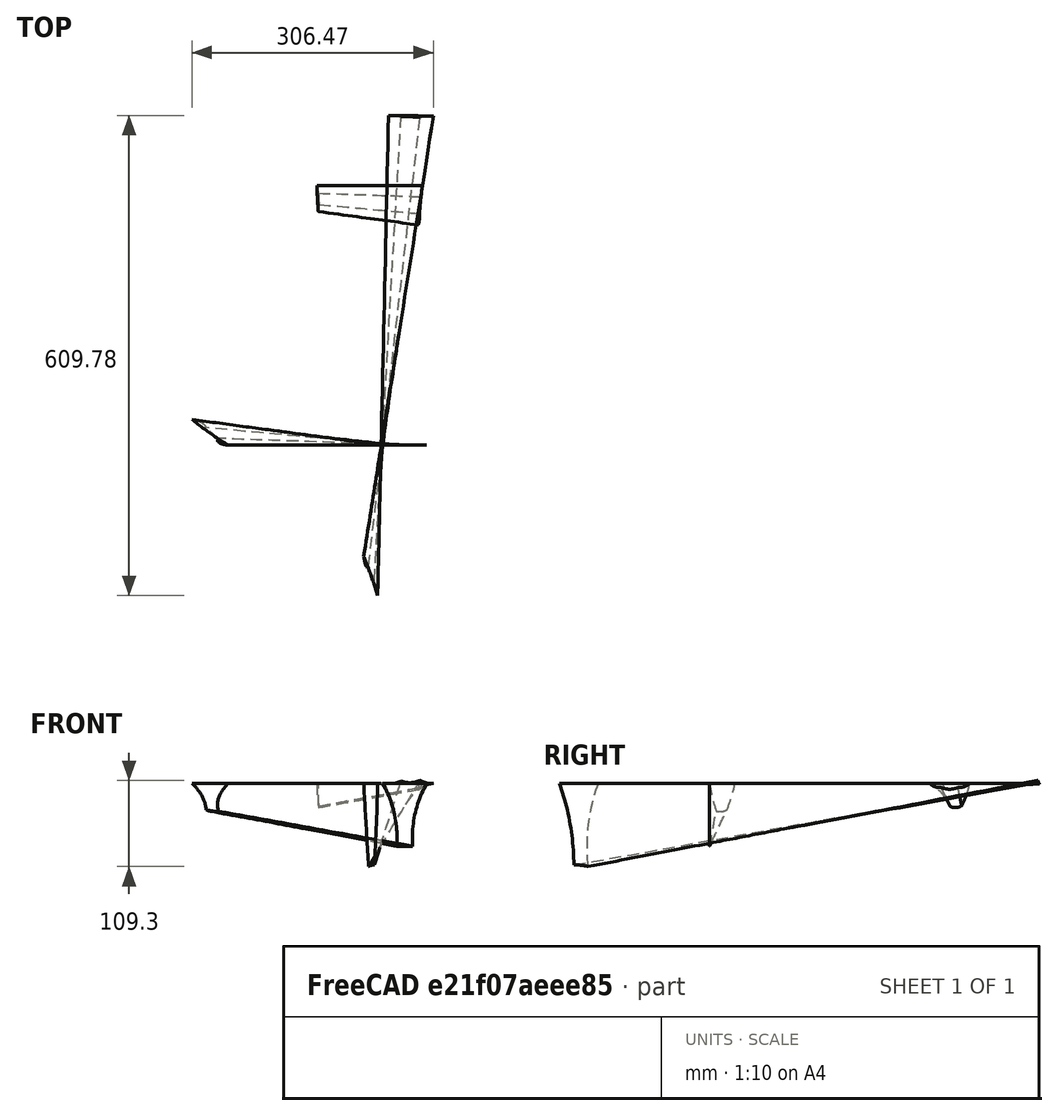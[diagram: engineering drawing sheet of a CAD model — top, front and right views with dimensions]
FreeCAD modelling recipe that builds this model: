
FCSTD DOCUMENT  (FreeCAD 0.19R24291 (Git))
Label: Neck
License: All rights reserved
LicenseURL: http://en.wikipedia.org/wiki/All_rights_reserved
objects: Sketcher::SketchObject×5, PartDesign::Body×1, Part::Sweep×1
note: 7 computed .brp shape members not serialized (recipe doc carries the construction recipe); baked Part::Feature solids carry a one-line shape summary decoded from their .brp

FEATURE [Sketcher::SketchObject] Sketch001  label="Neck_Profile_001"
  FullyConstrained = true
  Placement = pos=(0,0,0) rot=(1,0,0;1.5708rad)
  sketch-geometry (10):
    g0: GeomPoint X=-28 Y=-1.56319e-11 Z=0
    g1: GeomPoint X=28 Y=-1.56746e-11 Z=0
    g2: LineSegment StartX=-28 StartY=-1.56319e-11 StartZ=0 EndX=28 EndY=-1.56746e-11 EndZ=0
    g3: GeomPoint X=-10 Y=-80 Z=0
    g4: GeomPoint X=10 Y=-80 Z=0
    g5: LineSegment StartX=-10 StartY=-80 StartZ=0 EndX=10 EndY=-80 EndZ=0
    g6: GeomPoint X=-10 Y=-60 Z=0
    g7: GeomPoint X=10 Y=-60 Z=0
    g8: ArcOfCircle CenterX=-152.333 CenterY=-70 CenterZ=0 NormalX=0 NormalY=0 NormalZ=1 AngleXU=0 Radius=142.684 StartAngle=6.21304 EndAngle=6.79596
    g9: ArcOfCircle CenterX=152.333 CenterY=-70 CenterZ=0 NormalX=0 NormalY=0 NormalZ=1 AngleXU=0 Radius=142.684 StartAngle=2.62882 EndAngle=3.21174
  constraints (19):
    c: Symmetric(g0,g1,g-2)
    c: Coincident(g2,g0)
    c: Coincident(g2,g1)
    c: Distance(g2) = 56  'Heel_Neck_Width'
    c: Coincident(g5,g3)
    c: Coincident(g5,g4)
    c: Symmetric(g5,g5,g-2)
    c: Distance(g5) = 20  'Heel_Plate_Width'
    c: Symmetric(g6,g7,g-2)
    c: Coincident(g8,g5)
    c: Coincident(g8,g2)
    c: PointOnObject(g6,g8)
    c: Coincident(g9,g5)
    c: Coincident(g9,g2)
    c: PointOnObject(g7,g9)
    c: DistanceX(g6,g7) = 20  'Heel_Vertical_Curve'
    c: DistanceY(g6,g-1) = 60
    c: DistanceY(g5,g2) = 80  'Heel_Height'
    c: DistanceY(g-1,g2) = 0
FEATURE [Sketcher::SketchObject] Sketch002  label="Neck_Profile_002"
  FullyConstrained = true
  Placement = pos=(0,20,0) rot=(1,0,0;1.5708rad)
  sketch-geometry (10):
    g0: GeomPoint X=-28 Y=-2.0322e-12 Z=0
    g1: GeomPoint X=28 Y=-2.0179e-12 Z=0
    g2: LineSegment StartX=-28 StartY=-2.0322e-12 StartZ=0 EndX=28 EndY=-2.0179e-12 EndZ=0
    g3: GeomPoint X=-0.5 Y=-80 Z=0
    g4: GeomPoint X=0.5 Y=-80 Z=0
    g5: LineSegment StartX=-0.5 StartY=-80 StartZ=0 EndX=0.5 EndY=-80 EndZ=0
    g6: GeomPoint X=-2.5 Y=-60 Z=0
    g7: GeomPoint X=2.5 Y=-60 Z=0
    g8: ArcOfCircle CenterX=-142.558 CenterY=-84.1058 CenterZ=0 NormalX=0 NormalY=0 NormalZ=1 AngleXU=0 Radius=142.117 StartAngle=0.0288941 EndAngle=0.633298
    g9: ArcOfCircle CenterX=142.558 CenterY=-84.1058 CenterZ=0 NormalX=0 NormalY=0 NormalZ=1 AngleXU=0 Radius=142.117 StartAngle=2.50829 EndAngle=3.1127
  constraints (19):
    c: Symmetric(g0,g1,g-2)
    c: Coincident(g2,g0)
    c: Coincident(g2,g1)
    c: Distance(g2) = 56  'Heel_Neck_Width'
    c: Coincident(g5,g3)
    c: Coincident(g5,g4)
    c: Symmetric(g5,g5,g-2)
    c: Distance(g5) = 1  'Heel_Plate_Width'
    c: Symmetric(g6,g7,g-2)
    c: Coincident(g8,g5)
    c: Coincident(g8,g2)
    c: PointOnObject(g6,g8)
    c: Coincident(g9,g5)
    c: Coincident(g9,g2)
    c: PointOnObject(g7,g9)
    c: DistanceX(g6,g7) = 5  'Heel_Vertical_Curve'
    c: DistanceY(g6,g-1) = 60
    c: DistanceY(g5,g2) = 80  'Heel_Height'
    c: DistanceY(g-1,g2) = 0
FEATURE [Sketcher::SketchObject] Sketch003  label="Neck_Profile_005"
  FullyConstrained = true
  Placement = pos=(0,50,0) rot=(1,0,0;1.5708rad)
  sketch-geometry (7):
    g0: GeomPoint X=-28 Y=1.936e-13 Z=0
    g1: GeomPoint X=28 Y=1.794e-13 Z=0
    g2: LineSegment StartX=-28 StartY=1.936e-13 StartZ=0 EndX=28 EndY=1.794e-13 EndZ=0
    g3: GeomPoint X=0 Y=-20 Z=0
    g4: ArcOfCircle CenterX=-8.7e-15 CenterY=9.6 CenterZ=0 NormalX=0 NormalY=0 NormalZ=1 AngleXU=0 Radius=29.6 StartAngle=3.47189 EndAngle=4.01033
    g5: ArcOfCircle CenterX=-8.7e-15 CenterY=9.6 CenterZ=0 NormalX=0 NormalY=0 NormalZ=1 AngleXU=0 Radius=29.6 StartAngle=5.41445 EndAngle=5.95289
    g6: ArcOfCircle CenterX=-8.7e-15 CenterY=9.6 CenterZ=0 NormalX=0 NormalY=0 NormalZ=1 AngleXU=0 Radius=29.6 StartAngle=4.01033 EndAngle=5.41445
  constraints (17):
    c: Symmetric(g0,g1,g-2)
    c: Coincident(g2,g0)
    c: Coincident(g2,g1)
    c: Distance(g2) = 56  'Heel_Neck_Width'
    c: DistanceY(g-1,g2) = 0
    c: DistanceX(g3) = 0
    c: DistanceY(g3) = -20
    c: Coincident(g4,g2)
    c: Coincident(g5,g4)
    c: Coincident(g5,g2)
    c: Symmetric(g5,g4,g-2)
    c: DistanceY(g4) = 9.6
    c: Coincident(g6,g4)
    c: Coincident(g6,g5)
    c: Coincident(g4,g6)
    c: PointOnObject(g3,g6)
    c: DistanceY(g5,g2) = 13
FEATURE [Sketcher::SketchObject] Sketch  label="Neck_Top"
  FullyConstrained = true
  MapMode = 5
  Support = -> [XY_Plane]
  sketch-geometry (8):
    g0: GeomPoint X=-22.5 Y=330 Z=0
    g1: GeomPoint X=-30 Y=0 Z=0
    g2: GeomPoint X=30 Y=0 Z=0
    g3: GeomPoint X=22.5 Y=330 Z=0
    g4: LineSegment StartX=-30 StartY=0 StartZ=0 EndX=-22.5 EndY=330 EndZ=0
    g5: LineSegment StartX=30 StartY=0 StartZ=0 EndX=22.5 EndY=330 EndZ=0
    g6: LineSegment StartX=-30 StartY=0 StartZ=0 EndX=30 EndY=0 EndZ=0
    g7: LineSegment StartX=-22.5 StartY=330 StartZ=0 EndX=22.5 EndY=330 EndZ=0
  constraints (14):
    c: Symmetric(g0,g3,g-2)
    c: Distance(g0,g3) = 45  'Neck_Width_Nut'
    c: Symmetric(g1,g2,g-2)
    c: Distance(g1,g2) = 60
    c: Coincident(g4,g1)
    c: Coincident(g4,g0)
    c: Coincident(g5,g2)
    c: Coincident(g5,g3)
    c: DistanceY(g5,g5) = 330
    c: DistanceY(g5) = 0
    c: Coincident(g6,g4)
    c: Coincident(g6,g5)
    c: Coincident(g7,g4)
    c: Coincident(g7,g5)
FEATURE [Sketcher::SketchObject] Sketch004  label="Neck_Profile_006"
  FullyConstrained = true
  Placement = pos=(0,330,0) rot=(1,0,0;1.5708rad)
  sketch-geometry (7):
    g0: GeomPoint X=-22.5 Y=-3.6e-15 Z=0
    g1: GeomPoint X=22.5 Y=8.9e-15 Z=0
    g2: LineSegment StartX=-22.5 StartY=-3.6e-15 StartZ=0 EndX=22.5 EndY=8.9e-15 EndZ=0
    g3: GeomPoint X=0 Y=-15 Z=0
    g4: ArcOfCircle CenterX=-8e-16 CenterY=9.375 CenterZ=0 NormalX=0 NormalY=0 NormalZ=1 AngleXU=0 Radius=24.375 StartAngle=3.53638 EndAngle=4.30447
    g5: ArcOfCircle CenterX=-8e-16 CenterY=9.375 CenterZ=0 NormalX=0 NormalY=0 NormalZ=1 AngleXU=0 Radius=24.375 StartAngle=5.12031 EndAngle=5.88839
    g6: ArcOfCircle CenterX=-8e-16 CenterY=9.375 CenterZ=0 NormalX=0 NormalY=0 NormalZ=1 AngleXU=0 Radius=24.375 StartAngle=4.30447 EndAngle=5.12031
  constraints (17):
    c: Symmetric(g0,g1,g-2)
    c: Coincident(g2,g0)
    c: Coincident(g2,g1)
    c: Distance(g2) = 45  'Heel_Neck_Width'
    c: DistanceY(g-1,g2) = 0
    c: DistanceX(g3) = 0
    c: DistanceY(g3) = -15
    c: Coincident(g4,g2)
    c: Coincident(g5,g4)
    c: Coincident(g5,g2)
    c: Symmetric(g5,g4,g-2)
    c: DistanceY(g4) = 9.375
    c: Coincident(g6,g4)
    c: Coincident(g6,g5)
    c: Coincident(g4,g6)
    c: PointOnObject(g3,g6)
    c: DistanceY(g5,g2) = 13
FEATURE [PartDesign::Body] Body  label="Guitar_Neck"
  Group = -> [Sketch001,Sketch002,Sketch003,Sketch004,Sketch]
  Origin = -> Origin
FEATURE [Part::Sweep] Sweep
  Frenet = false
  Sections = -> [Sketch001,Sketch004]
  Solid = false
  Spine = -> Sketch [Edge2,Edge4,Edge1,Edge3]
  Transition = 1
